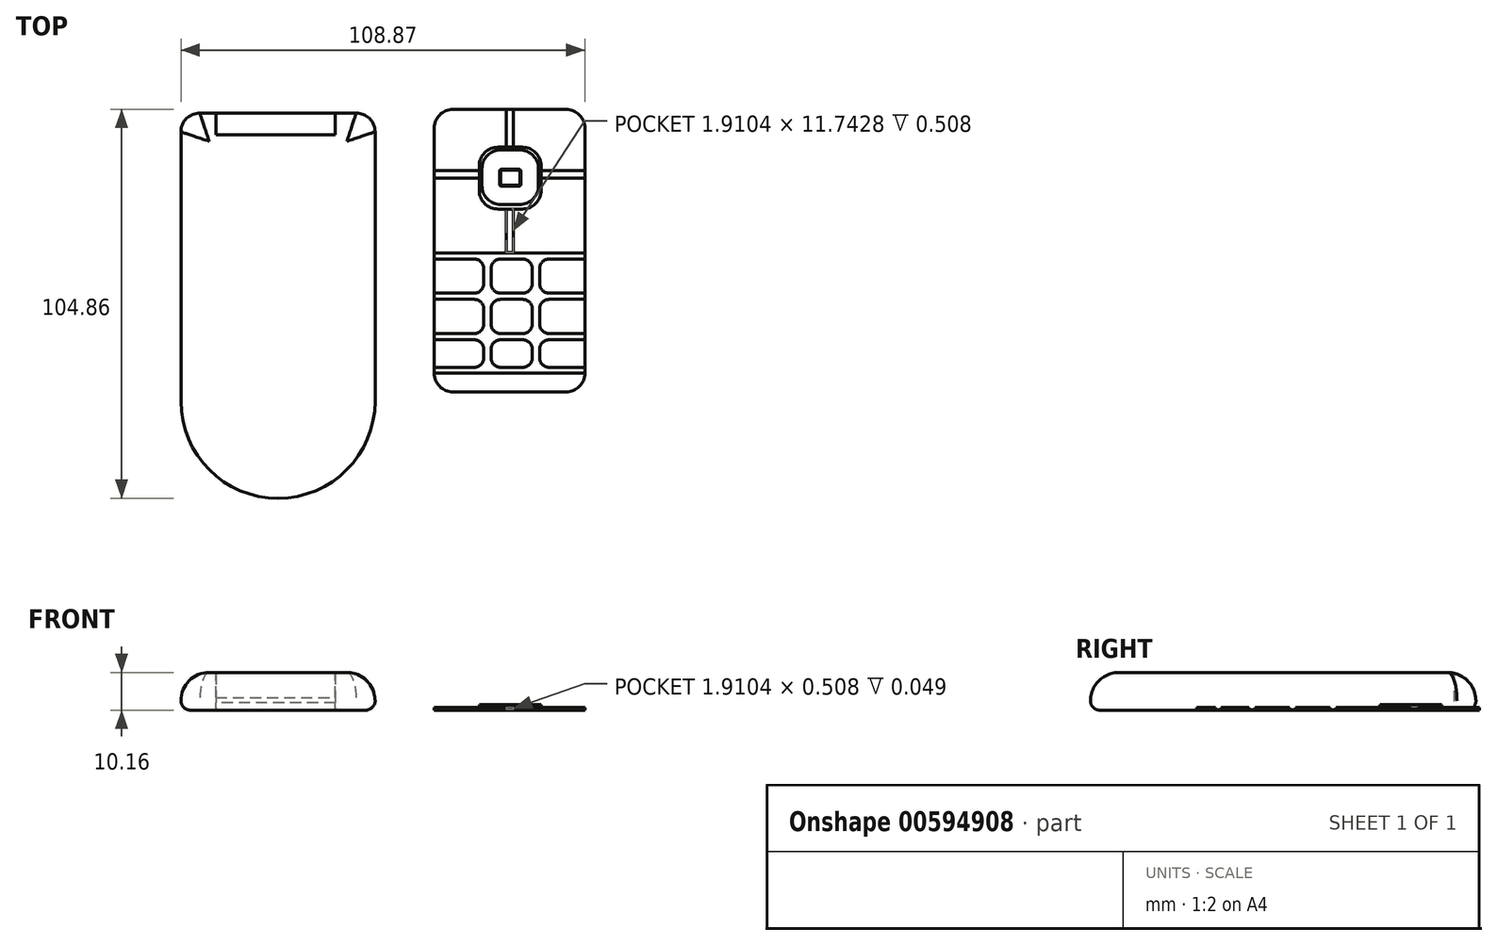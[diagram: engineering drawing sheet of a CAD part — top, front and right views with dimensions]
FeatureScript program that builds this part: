
annotation { "Feature Type Name" : "Feature", "Feature Type Description" : "" }
export const myFeature = defineFeature(function(context is Context, id is Id, definition is map)
    precondition{}
    {
        {
            var Q0;
            Q0=qCreatedBy(makeId("Top.planeOp"),FACE);
            var sketch = newSketch(context, id + "F0", { "sketchPlane" : qUnion([Q0])});
            skLineSegment(sketch, "E0.bottom", {"start": v(-38.75, 53.9) * mm, "end": v(13.57, 53.9) * mm});
            skLineSegment(sketch, "E0.top", {"start": v(-38.75, -49.98) * mm, "end": v(13.57, -49.98) * mm});
            skLineSegment(sketch, "E0.left", {"start": v(-38.75, 53.9) * mm, "end": v(-38.75, -49.98) * mm});
            skLineSegment(sketch, "E0.right", {"start": v(13.57, 53.9) * mm, "end": v(13.57, -49.98) * mm});
            skSolve(sketch);
        }
        {
            var Q0;
            Q0=makeQuery(id+"F0.imprint","IMPRINT",FACE,{"disambiguationData":[TD([[makeQuery(id+"F0.imprint","IMPRINT",EDGE,{"derivedFrom":sQuery(id+"F0.wireOp",EDGE,"E0.bottom")}),-1.0]])]});
            extrude(context, id + "F1", {"entities" : qUnion([Q0]), "depth" : 10.16 * mm, "offsetDistance" : 25.4 * mm});
        }
        {
            var Q0;
            Q0=makeQuery(id+"F1.opExtrude","SWEPT_EDGE",EDGE,{"disambiguationData":[OSD([sQuery(id+"F0.wireOp",EDGE,"E0.top"),sQuery(id+"F0.wireOp",EDGE,"E0.left")])]});
            var Q1;
            Q1=makeQuery(id+"F1.opExtrude","SWEPT_EDGE",EDGE,{"disambiguationData":[OSD([sQuery(id+"F0.wireOp",EDGE,"E0.top"),sQuery(id+"F0.wireOp",EDGE,"E0.right")])]});
            fillet(context, id + "F2", {"entities" : qUnion([Q0, Q1]), "radius" : 26.16 * mm, "tangentPropagation" : true, "allowEdgeOverflow" : false});
        }
        {
            var Q0;
            Q0=makeQuery(id+"F1.opExtrude","SWEPT_EDGE",EDGE,{"disambiguationData":[OSD([sQuery(id+"F0.wireOp",EDGE,"E0.bottom"),sQuery(id+"F0.wireOp",EDGE,"E0.left")])]});
            var Q1;
            Q1=makeQuery(id+"F1.opExtrude","SWEPT_EDGE",EDGE,{"disambiguationData":[OSD([sQuery(id+"F0.wireOp",EDGE,"E0.bottom"),sQuery(id+"F0.wireOp",EDGE,"E0.right")])]});
            fillet(context, id + "F3", {"entities" : qUnion([Q0, Q1]), "radius" : 5.08 * mm, "tangentPropagation" : true, "allowEdgeOverflow" : false});
        }
        {
            var Q0;
            Q0=makeQuery(id+"F1.opExtrude","CAP_EDGE",EDGE,{"disambiguationData":[OSD([sQuery(id+"F0.wireOp",EDGE,"E0.right")])],"isStart":false});
            fillet(context, id + "F4", {"entities" : qUnion([Q0]), "radius" : 7.62 * mm, "tangentPropagation" : true, "allowEdgeOverflow" : false});
        }
        {
            var Q0;
            Q0=makeQuery(id+"F1.opExtrude","CAP_EDGE",EDGE,{"disambiguationData":[OSD([sQuery(id+"F0.wireOp",EDGE,"E0.right")])],"isStart":true});
            fillet(context, id + "F5", {"entities" : qUnion([Q0]), "radius" : 2.54 * mm, "tangentPropagation" : true, "allowEdgeOverflow" : false});
        }
        {
            var Q0;
            Q0=qCreatedBy(makeId("Top.planeOp"),FACE);
            var sketch = newSketch(context, id + "F6", { "sketchPlane" : qUnion([Q0])});
            skLineSegment(sketch, "E1.bottom", {"start": v(29.48, -21.32) * mm, "end": v(70.12, -21.32) * mm});
            skLineSegment(sketch, "E1.top", {"start": v(29.48, 54.88) * mm, "end": v(70.12, 54.88) * mm});
            skLineSegment(sketch, "E1.left", {"start": v(29.48, -21.32) * mm, "end": v(29.48, 54.88) * mm});
            skLineSegment(sketch, "E1.right", {"start": v(70.12, -21.32) * mm, "end": v(70.12, 54.88) * mm});
            skSolve(sketch);
        }
        {
            var Q0;
            Q0=makeQuery(id+"F6.imprint","IMPRINT",FACE,{"disambiguationData":[TD([[makeQuery(id+"F6.imprint","IMPRINT",EDGE,{"derivedFrom":sQuery(id+"F6.wireOp",EDGE,"E1.bottom")}),1.0]])]});
            extrude(context, id + "F7", {"entities" : qUnion([Q0]), "depth" : 0.76 * mm, "offsetDistance" : 25.4 * mm});
        }
        {
            var Q0;
            Q0=makeQuery(id+"F7.opExtrude","SWEPT_EDGE",EDGE,{"disambiguationData":[OSD([sQuery(id+"F6.wireOp",EDGE,"E1.top"),sQuery(id+"F6.wireOp",EDGE,"E1.left")])]});
            var Q1;
            Q1=makeQuery(id+"F7.opExtrude","SWEPT_EDGE",EDGE,{"disambiguationData":[OSD([sQuery(id+"F6.wireOp",EDGE,"E1.top"),sQuery(id+"F6.wireOp",EDGE,"E1.right")])]});
            var Q2;
            Q2=makeQuery(id+"F7.opExtrude","SWEPT_EDGE",EDGE,{"disambiguationData":[OSD([sQuery(id+"F6.wireOp",EDGE,"E1.bottom"),sQuery(id+"F6.wireOp",EDGE,"E1.left")])]});
            var Q3;
            Q3=makeQuery(id+"F7.opExtrude","SWEPT_EDGE",EDGE,{"disambiguationData":[OSD([sQuery(id+"F6.wireOp",EDGE,"E1.bottom"),sQuery(id+"F6.wireOp",EDGE,"E1.right")])]});
            fillet(context, id + "F8", {"entities" : qUnion([Q0, Q1, Q2, Q3]), "radius" : 5.08 * mm, "tangentPropagation" : true, "allowEdgeOverflow" : false});
        }
        {
            var Q0;
            Q0=makeQuery(id+"F7.opExtrude","CAP_FACE",FACE,{"disambiguationData":[OSD([sQuery(id+"F6.wireOp",EDGE,"E1.bottom"),sQuery(id+"F6.wireOp",EDGE,"E1.top"),sQuery(id+"F6.wireOp",EDGE,"E1.left"),sQuery(id+"F6.wireOp",EDGE,"E1.right")])],"isStart":false});
            var sketch = newSketch(context, id + "F9", { "sketchPlane" : qUnion([Q0])});
            skLineSegment(sketch, "E2", {"start": v(29.48, 16.2) * mm, "end": v(70.12, 16.2) * mm});
            skLineSegment(sketch, "E3", {"start": v(29.48, 5.31) * mm, "end": v(70.12, 5.31) * mm});
            skLineSegment(sketch, "E4", {"start": v(29.48, -5.57) * mm, "end": v(70.12, -5.57) * mm});
            skLineSegment(sketch, "E5", {"start": v(29.48, -16.24) * mm, "end": v(70.12, -16.24) * mm});
            skLineSegment(sketch, "E6", {"start": v(29.48, 14.53) * mm, "end": v(70.12, 14.53) * mm});
            skLineSegment(sketch, "E7", {"start": v(29.48, 3.64) * mm, "end": v(70.12, 3.64) * mm});
            skLineSegment(sketch, "E8", {"start": v(29.48, -7.24) * mm, "end": v(70.12, -7.24) * mm});
            skLineSegment(sketch, "E9", {"start": v(29.48, 16.2) * mm, "end": v(29.48, 14.53) * mm});
            skLineSegment(sketch, "E10", {"start": v(29.48, 5.31) * mm, "end": v(29.48, 3.64) * mm});
            skLineSegment(sketch, "E11", {"start": v(29.48, -5.57) * mm, "end": v(29.48, -7.24) * mm});
            skLineSegment(sketch, "E12", {"start": v(70.12, -5.57) * mm, "end": v(70.12, -7.24) * mm});
            skLineSegment(sketch, "E13", {"start": v(70.12, 5.31) * mm, "end": v(70.12, 3.64) * mm});
            skLineSegment(sketch, "E14", {"start": v(70.12, 16.2) * mm, "end": v(70.12, 14.53) * mm});
            skLineSegment(sketch, "E15", {"start": v(42.84, 16.2) * mm, "end": v(42.84, -16.24) * mm});
            skLineSegment(sketch, "E16", {"start": v(42.84, -16.24) * mm, "end": v(44.85, -16.24) * mm});
            skLineSegment(sketch, "E17", {"start": v(44.85, -16.24) * mm, "end": v(44.85, 16.2) * mm});
            skLineSegment(sketch, "E18", {"start": v(44.85, 16.2) * mm, "end": v(55.9, 16.2) * mm});
            skLineSegment(sketch, "E19", {"start": v(55.9, 16.2) * mm, "end": v(55.9, -16.24) * mm});
            skLineSegment(sketch, "E20", {"start": v(55.9, -16.24) * mm, "end": v(57.92, -16.24) * mm});
            skLineSegment(sketch, "E21", {"start": v(57.92, -16.24) * mm, "end": v(57.92, 16.2) * mm});
            skLineSegment(sketch, "E22", {"start": v(55.9, 16.2) * mm, "end": v(57.92, 16.2) * mm});
            skLineSegment(sketch, "E23", {"start": v(44.85, 16.2) * mm, "end": v(42.84, 16.2) * mm});
            skLineSegment(sketch, "E24", {"start": v(55.9, -16.24) * mm, "end": v(55.9, -19.8) * mm});
            skLineSegment(sketch, "E25", {"start": v(55.9, -19.8) * mm, "end": v(57.92, -16.24) * mm});
            skLineSegment(sketch, "E26", {"start": v(42.84, -16.24) * mm, "end": v(42.84, -19.8) * mm});
            skLineSegment(sketch, "E27", {"start": v(42.84, -19.8) * mm, "end": v(44.85, -16.24) * mm});
            skLineSegment(sketch, "E28", {"start": v(29.48, -14.7) * mm, "end": v(70.12, -14.7) * mm});
            skLineSegment(sketch, "E29", {"start": v(29.48, -14.7) * mm, "end": v(29.48, -16.24) * mm});
            skLineSegment(sketch, "E30", {"start": v(70.12, -14.7) * mm, "end": v(70.12, -16.24) * mm});
            skSolve(sketch);
        }
        {
            var Q0;
            {var subQ0=sQuery(id+"F9.wireOp",EDGE,"E9");Q0=makeQuery(id+"F9.imprint","IMPRINT",FACE,{"disambiguationData":[TD([[makeQuery(id+"F9.imprint","IMPRINT",EDGE,{"derivedFrom":subQ0}),-1.0]])]});}
            var Q1;
            {var subQ0=sQuery(id+"F9.wireOp",EDGE,"E17");var subQ1=sQuery(id+"F9.wireOp",EDGE,"E2");var subQ2=makeQuery(id+"F9.imprint","INTERSECT",VERTEX,{"derivedFrom":[subQ1,subQ0]});Q1=makeQuery(id+"F9.imprint","IMPRINT",FACE,{"disambiguationData":[TD([[makeQuery(id+"F9.imprint","IMPRINT",EDGE,{"disambiguationData":[TD([[subQ2,-1.0]])],"derivedFrom":subQ1}),-1.0]])]});}
            var Q2;
            {var subQ0=sQuery(id+"F9.wireOp",EDGE,"E14");Q2=makeQuery(id+"F9.imprint","IMPRINT",FACE,{"disambiguationData":[TD([[makeQuery(id+"F9.imprint","IMPRINT",EDGE,{"derivedFrom":subQ0}),1.0]])]});}
            var Q3;
            {var subQ0=sQuery(id+"F9.wireOp",EDGE,"E13");Q3=makeQuery(id+"F9.imprint","IMPRINT",FACE,{"disambiguationData":[TD([[makeQuery(id+"F9.imprint","IMPRINT",EDGE,{"derivedFrom":subQ0}),1.0]])]});}
            var Q4;
            {var subQ0=sQuery(id+"F9.wireOp",EDGE,"E17");var subQ1=sQuery(id+"F9.wireOp",EDGE,"E3");var subQ2=makeQuery(id+"F9.imprint","INTERSECT",VERTEX,{"derivedFrom":[subQ1,subQ0]});Q4=makeQuery(id+"F9.imprint","IMPRINT",FACE,{"disambiguationData":[TD([[makeQuery(id+"F9.imprint","IMPRINT",EDGE,{"disambiguationData":[TD([[subQ2,-1.0]])],"derivedFrom":subQ1}),-1.0]])]});}
            var Q5;
            {var subQ0=sQuery(id+"F9.wireOp",EDGE,"E10");Q5=makeQuery(id+"F9.imprint","IMPRINT",FACE,{"disambiguationData":[TD([[makeQuery(id+"F9.imprint","IMPRINT",EDGE,{"derivedFrom":subQ0}),-1.0]])]});}
            var Q6;
            {var subQ0=sQuery(id+"F9.wireOp",EDGE,"E11");Q6=makeQuery(id+"F9.imprint","IMPRINT",FACE,{"disambiguationData":[TD([[makeQuery(id+"F9.imprint","IMPRINT",EDGE,{"derivedFrom":subQ0}),-1.0]])]});}
            var Q7;
            {var subQ0=sQuery(id+"F9.wireOp",EDGE,"E17");var subQ1=sQuery(id+"F9.wireOp",EDGE,"E4");var subQ2=makeQuery(id+"F9.imprint","INTERSECT",VERTEX,{"derivedFrom":[subQ1,subQ0]});Q7=makeQuery(id+"F9.imprint","IMPRINT",FACE,{"disambiguationData":[TD([[makeQuery(id+"F9.imprint","IMPRINT",EDGE,{"disambiguationData":[TD([[subQ2,-1.0]])],"derivedFrom":subQ1}),-1.0]])]});}
            var Q8;
            {var subQ3=sQuery(id+"F9.wireOp",EDGE,"E12");Q8=makeQuery(id+"F9.imprint","IMPRINT",FACE,{"disambiguationData":[TD([[makeQuery(id+"F9.imprint","IMPRINT",EDGE,{"derivedFrom":subQ3}),1.0]])]});}
            var Q9;
            {var subQ0=sQuery(id+"F9.wireOp",EDGE,"E21");var subQ1=sQuery(id+"F9.wireOp",EDGE,"E4");var subQ2=makeQuery(id+"F9.imprint","INTERSECT",VERTEX,{"derivedFrom":[subQ1,subQ0]});Q9=makeQuery(id+"F9.imprint","IMPRINT",FACE,{"disambiguationData":[TD([[makeQuery(id+"F9.imprint","IMPRINT",EDGE,{"disambiguationData":[TD([[subQ2,1.0]])],"derivedFrom":subQ1}),1.0]])]});}
            var Q10;
            {var subQ0=sQuery(id+"F9.wireOp",EDGE,"E21");var subQ1=sQuery(id+"F9.wireOp",EDGE,"E4");var subQ2=makeQuery(id+"F9.imprint","INTERSECT",VERTEX,{"derivedFrom":[subQ1,subQ0]});Q10=makeQuery(id+"F9.imprint","IMPRINT",FACE,{"disambiguationData":[TD([[makeQuery(id+"F9.imprint","IMPRINT",EDGE,{"disambiguationData":[TD([[subQ2,1.0]])],"derivedFrom":subQ1}),-1.0]])]});}
            var Q11;
            {var subQ5=sQuery(id+"F9.wireOp",EDGE,"E20");Q11=makeQuery(id+"F9.imprint","IMPRINT",FACE,{"disambiguationData":[TD([[makeQuery(id+"F9.imprint","IMPRINT",EDGE,{"derivedFrom":subQ5}),1.0]])]});}
            var Q12;
            {var subQ0=sQuery(id+"F9.wireOp",EDGE,"E21");var subQ1=sQuery(id+"F9.wireOp",EDGE,"E3");var subQ2=makeQuery(id+"F9.imprint","INTERSECT",VERTEX,{"derivedFrom":[subQ1,subQ0]});Q12=makeQuery(id+"F9.imprint","IMPRINT",FACE,{"disambiguationData":[TD([[makeQuery(id+"F9.imprint","IMPRINT",EDGE,{"disambiguationData":[TD([[subQ2,1.0]])],"derivedFrom":subQ1}),-1.0]])]});}
            var Q13;
            {var subQ0=sQuery(id+"F9.wireOp",EDGE,"E21");var subQ1=sQuery(id+"F9.wireOp",EDGE,"E3");var subQ2=makeQuery(id+"F9.imprint","INTERSECT",VERTEX,{"derivedFrom":[subQ1,subQ0]});Q13=makeQuery(id+"F9.imprint","IMPRINT",FACE,{"disambiguationData":[TD([[makeQuery(id+"F9.imprint","IMPRINT",EDGE,{"disambiguationData":[TD([[subQ2,1.0]])],"derivedFrom":subQ1}),1.0]])]});}
            var Q14;
            {var subQ0=sQuery(id+"F9.wireOp",EDGE,"E21");var subQ1=sQuery(id+"F9.wireOp",EDGE,"E2");var subQ2=makeQuery(id+"F9.imprint","INTERSECT",VERTEX,{"derivedFrom":[subQ1,subQ0]});Q14=makeQuery(id+"F9.imprint","IMPRINT",FACE,{"disambiguationData":[TD([[makeQuery(id+"F9.imprint","IMPRINT",EDGE,{"disambiguationData":[TD([[subQ2,1.0]])],"derivedFrom":subQ1}),-1.0]])]});}
            var Q15;
            {var subQ0=sQuery(id+"F9.wireOp",EDGE,"E17");var subQ1=sQuery(id+"F9.wireOp",EDGE,"E2");var subQ2=makeQuery(id+"F9.imprint","INTERSECT",VERTEX,{"derivedFrom":[subQ1,subQ0]});Q15=makeQuery(id+"F9.imprint","IMPRINT",FACE,{"disambiguationData":[TD([[makeQuery(id+"F9.imprint","IMPRINT",EDGE,{"disambiguationData":[TD([[subQ2,1.0]])],"derivedFrom":subQ1}),-1.0]])]});}
            var Q16;
            {var subQ0=sQuery(id+"F9.wireOp",EDGE,"E17");var subQ1=sQuery(id+"F9.wireOp",EDGE,"E3");var subQ2=makeQuery(id+"F9.imprint","INTERSECT",VERTEX,{"derivedFrom":[subQ1,subQ0]});Q16=makeQuery(id+"F9.imprint","IMPRINT",FACE,{"disambiguationData":[TD([[makeQuery(id+"F9.imprint","IMPRINT",EDGE,{"disambiguationData":[TD([[subQ2,1.0]])],"derivedFrom":subQ1}),1.0]])]});}
            var Q17;
            {var subQ0=sQuery(id+"F9.wireOp",EDGE,"E17");var subQ1=sQuery(id+"F9.wireOp",EDGE,"E3");var subQ2=makeQuery(id+"F9.imprint","INTERSECT",VERTEX,{"derivedFrom":[subQ1,subQ0]});Q17=makeQuery(id+"F9.imprint","IMPRINT",FACE,{"disambiguationData":[TD([[makeQuery(id+"F9.imprint","IMPRINT",EDGE,{"disambiguationData":[TD([[subQ2,1.0]])],"derivedFrom":subQ1}),-1.0]])]});}
            var Q18;
            {var subQ0=sQuery(id+"F9.wireOp",EDGE,"E15");var subQ1=sQuery(id+"F9.wireOp",EDGE,"E4");var subQ2=makeQuery(id+"F9.imprint","INTERSECT",VERTEX,{"derivedFrom":[subQ1,subQ0]});Q18=makeQuery(id+"F9.imprint","IMPRINT",FACE,{"disambiguationData":[TD([[makeQuery(id+"F9.imprint","IMPRINT",EDGE,{"disambiguationData":[TD([[subQ2,-1.0]])],"derivedFrom":subQ1}),1.0]])]});}
            var Q19;
            {var subQ0=sQuery(id+"F9.wireOp",EDGE,"E15");var subQ1=sQuery(id+"F9.wireOp",EDGE,"E4");var subQ2=makeQuery(id+"F9.imprint","INTERSECT",VERTEX,{"derivedFrom":[subQ1,subQ0]});Q19=makeQuery(id+"F9.imprint","IMPRINT",FACE,{"disambiguationData":[TD([[makeQuery(id+"F9.imprint","IMPRINT",EDGE,{"disambiguationData":[TD([[subQ2,-1.0]])],"derivedFrom":subQ1}),-1.0]])]});}
            var Q20;
            {var subQ5=sQuery(id+"F9.wireOp",EDGE,"E16");Q20=makeQuery(id+"F9.imprint","IMPRINT",FACE,{"disambiguationData":[TD([[makeQuery(id+"F9.imprint","IMPRINT",EDGE,{"derivedFrom":subQ5}),1.0]])]});}
            var Q21;
            {var subQ0=sQuery(id+"F9.wireOp",EDGE,"E29");Q21=makeQuery(id+"F9.imprint","IMPRINT",FACE,{"disambiguationData":[TD([[makeQuery(id+"F9.imprint","IMPRINT",EDGE,{"derivedFrom":subQ0}),-1.0]])]});}
            var Q22;
            {var subQ0=sQuery(id+"F9.wireOp",EDGE,"E17");var subQ1=sQuery(id+"F9.wireOp",EDGE,"E8");var subQ2=makeQuery(id+"F9.imprint","INTERSECT",VERTEX,{"derivedFrom":[subQ1,subQ0]});Q22=makeQuery(id+"F9.imprint","IMPRINT",FACE,{"disambiguationData":[TD([[makeQuery(id+"F9.imprint","IMPRINT",EDGE,{"disambiguationData":[TD([[subQ2,1.0]])],"derivedFrom":subQ1}),-1.0]])]});}
            var Q23;
            {var subQ0=sQuery(id+"F9.wireOp",EDGE,"E17");var subQ5=sQuery(id+"F9.wireOp",EDGE,"E28");var subQ6=makeQuery(id+"F9.imprint","INTERSECT",VERTEX,{"derivedFrom":[subQ0,subQ5]});Q23=makeQuery(id+"F9.imprint","IMPRINT",FACE,{"disambiguationData":[TD([[makeQuery(id+"F9.imprint","IMPRINT",EDGE,{"disambiguationData":[TD([[subQ6,1.0]])],"derivedFrom":subQ5}),-1.0]])]});}
            var Q24;
            {var subQ0=sQuery(id+"F9.wireOp",EDGE,"E17");var subQ5=sQuery(id+"F9.wireOp",EDGE,"E28");var subQ6=makeQuery(id+"F9.imprint","INTERSECT",VERTEX,{"derivedFrom":[subQ0,subQ5]});Q24=makeQuery(id+"F9.imprint","IMPRINT",FACE,{"disambiguationData":[TD([[makeQuery(id+"F9.imprint","IMPRINT",EDGE,{"disambiguationData":[TD([[subQ6,-1.0]])],"derivedFrom":subQ5}),-1.0]])]});}
            var Q25;
            {var subQ3=sQuery(id+"F9.wireOp",EDGE,"E21");var subQ5=sQuery(id+"F9.wireOp",EDGE,"E28");var subQ6=makeQuery(id+"F9.imprint","INTERSECT",VERTEX,{"derivedFrom":[subQ3,subQ5]});Q25=makeQuery(id+"F9.imprint","IMPRINT",FACE,{"disambiguationData":[TD([[makeQuery(id+"F9.imprint","IMPRINT",EDGE,{"disambiguationData":[TD([[subQ6,1.0]])],"derivedFrom":subQ5}),-1.0]])]});}
            var Q26;
            {var subQ0=sQuery(id+"F9.wireOp",EDGE,"E21");var subQ1=sQuery(id+"F9.wireOp",EDGE,"E8");var subQ2=makeQuery(id+"F9.imprint","INTERSECT",VERTEX,{"derivedFrom":[subQ1,subQ0]});Q26=makeQuery(id+"F9.imprint","IMPRINT",FACE,{"disambiguationData":[TD([[makeQuery(id+"F9.imprint","IMPRINT",EDGE,{"disambiguationData":[TD([[subQ2,1.0]])],"derivedFrom":subQ1}),-1.0]])]});}
            var Q27;
            {var subQ0=sQuery(id+"F9.wireOp",EDGE,"E30");Q27=makeQuery(id+"F9.imprint","IMPRINT",FACE,{"disambiguationData":[TD([[makeQuery(id+"F9.imprint","IMPRINT",EDGE,{"derivedFrom":subQ0}),1.0]])]});}
            extrude(context, id + "F10", {"entities" : qUnion([Q0, Q1, Q2, Q3, Q4, Q5, Q6, Q7, Q8, Q9, Q10, Q11, Q12, Q13, Q14, Q15, Q16, Q17, Q18, Q19, Q20, Q21, Q22, Q23, Q24, Q25, Q26, Q27]), "operationType" : NewBodyOperationType.REMOVE, "oppositeDirection" : true, "depth" : 0.6 * mm, "offsetDistance" : 25.4 * mm});
        }
        {
            var Q0;
            Q0=makeQuery(id+"F10.boolean.opBoolean","COPY",EDGE,{"derivedFrom":makeQuery(id+"F10.opExtrude","SWEPT_EDGE",EDGE,{"disambiguationData":[OSD([sQuery(id+"F6.wireOp",EDGE,"E1.right"),sQuery(id+"F9.wireOp",EDGE,"E28"),sQuery(id+"F9.wireOp",EDGE,"E30")])]})});
            var Q1;
            Q1=makeQuery(id+"F10.boolean.opBoolean","COPY",EDGE,{"derivedFrom":makeQuery(id+"F10.opExtrude","SWEPT_EDGE",EDGE,{"disambiguationData":[OSD([sQuery(id+"F6.wireOp",EDGE,"E1.right"),sQuery(id+"F9.wireOp",EDGE,"E4"),sQuery(id+"F9.wireOp",EDGE,"E12")])]})});
            var Q2;
            Q2=makeQuery(id+"F10.boolean.opBoolean","COPY",EDGE,{"derivedFrom":makeQuery(id+"F10.opExtrude","SWEPT_EDGE",EDGE,{"disambiguationData":[OSD([sQuery(id+"F9.wireOp",EDGE,"E19"),sQuery(id+"F9.wireOp",EDGE,"E28")])]})});
            var Q3;
            Q3=makeQuery(id+"F10.boolean.opBoolean","COPY",EDGE,{"derivedFrom":makeQuery(id+"F10.opExtrude","SWEPT_EDGE",EDGE,{"disambiguationData":[OSD([sQuery(id+"F9.wireOp",EDGE,"E4"),sQuery(id+"F9.wireOp",EDGE,"E19")])]})});
            var Q4;
            Q4=makeQuery(id+"F10.boolean.opBoolean","COPY",EDGE,{"derivedFrom":makeQuery(id+"F10.opExtrude","SWEPT_EDGE",EDGE,{"disambiguationData":[OSD([sQuery(id+"F9.wireOp",EDGE,"E7"),sQuery(id+"F9.wireOp",EDGE,"E19")])]})});
            var Q5;
            Q5=makeQuery(id+"F10.boolean.opBoolean","COPY",EDGE,{"derivedFrom":makeQuery(id+"F10.opExtrude","SWEPT_EDGE",EDGE,{"disambiguationData":[OSD([sQuery(id+"F9.wireOp",EDGE,"E3"),sQuery(id+"F9.wireOp",EDGE,"E19")])]})});
            var Q6;
            Q6=makeQuery(id+"F10.boolean.opBoolean","COPY",EDGE,{"derivedFrom":makeQuery(id+"F10.opExtrude","SWEPT_EDGE",EDGE,{"disambiguationData":[OSD([sQuery(id+"F9.wireOp",EDGE,"E6"),sQuery(id+"F9.wireOp",EDGE,"E19")])]})});
            var Q7;
            Q7=makeQuery(id+"F10.boolean.opBoolean","COPY",EDGE,{"derivedFrom":makeQuery(id+"F10.opExtrude","SWEPT_EDGE",EDGE,{"disambiguationData":[OSD([sQuery(id+"F9.wireOp",EDGE,"E15"),sQuery(id+"F9.wireOp",EDGE,"E28")])]})});
            var Q8;
            Q8=makeQuery(id+"F10.boolean.opBoolean","COPY",EDGE,{"derivedFrom":makeQuery(id+"F10.opExtrude","SWEPT_EDGE",EDGE,{"disambiguationData":[OSD([sQuery(id+"F9.wireOp",EDGE,"E4"),sQuery(id+"F9.wireOp",EDGE,"E15")])]})});
            var Q9;
            Q9=makeQuery(id+"F10.boolean.opBoolean","COPY",EDGE,{"derivedFrom":makeQuery(id+"F10.opExtrude","SWEPT_EDGE",EDGE,{"disambiguationData":[OSD([sQuery(id+"F9.wireOp",EDGE,"E7"),sQuery(id+"F9.wireOp",EDGE,"E15")])]})});
            var Q10;
            Q10=makeQuery(id+"F10.boolean.opBoolean","COPY",EDGE,{"derivedFrom":makeQuery(id+"F10.opExtrude","SWEPT_EDGE",EDGE,{"disambiguationData":[OSD([sQuery(id+"F9.wireOp",EDGE,"E3"),sQuery(id+"F9.wireOp",EDGE,"E15")])]})});
            var Q11;
            Q11=makeQuery(id+"F10.boolean.opBoolean","COPY",EDGE,{"derivedFrom":makeQuery(id+"F10.opExtrude","SWEPT_EDGE",EDGE,{"disambiguationData":[OSD([sQuery(id+"F9.wireOp",EDGE,"E3"),sQuery(id+"F9.wireOp",EDGE,"E17")])]})});
            var Q12;
            Q12=makeQuery(id+"F10.boolean.opBoolean","COPY",EDGE,{"derivedFrom":makeQuery(id+"F10.opExtrude","SWEPT_EDGE",EDGE,{"disambiguationData":[OSD([sQuery(id+"F9.wireOp",EDGE,"E4"),sQuery(id+"F9.wireOp",EDGE,"E17")])]})});
            var Q13;
            Q13=makeQuery(id+"F10.boolean.opBoolean","COPY",EDGE,{"derivedFrom":makeQuery(id+"F10.opExtrude","SWEPT_EDGE",EDGE,{"disambiguationData":[OSD([sQuery(id+"F9.wireOp",EDGE,"E17"),sQuery(id+"F9.wireOp",EDGE,"E28")])]})});
            var Q14;
            Q14=makeQuery(id+"F10.boolean.opBoolean","COPY",EDGE,{"derivedFrom":makeQuery(id+"F10.opExtrude","SWEPT_EDGE",EDGE,{"disambiguationData":[OSD([sQuery(id+"F6.wireOp",EDGE,"E1.left"),sQuery(id+"F9.wireOp",EDGE,"E28"),sQuery(id+"F9.wireOp",EDGE,"E29")])]})});
            var Q15;
            Q15=makeQuery(id+"F10.boolean.opBoolean","COPY",EDGE,{"derivedFrom":makeQuery(id+"F10.opExtrude","SWEPT_EDGE",EDGE,{"disambiguationData":[OSD([sQuery(id+"F9.wireOp",EDGE,"E21"),sQuery(id+"F9.wireOp",EDGE,"E28")])]})});
            var Q16;
            Q16=makeQuery(id+"F10.boolean.opBoolean","COPY",EDGE,{"derivedFrom":makeQuery(id+"F10.opExtrude","SWEPT_EDGE",EDGE,{"disambiguationData":[OSD([sQuery(id+"F9.wireOp",EDGE,"E4"),sQuery(id+"F9.wireOp",EDGE,"E21")])]})});
            var Q17;
            Q17=makeQuery(id+"F10.boolean.opBoolean","COPY",EDGE,{"derivedFrom":makeQuery(id+"F10.opExtrude","SWEPT_EDGE",EDGE,{"disambiguationData":[OSD([sQuery(id+"F9.wireOp",EDGE,"E3"),sQuery(id+"F9.wireOp",EDGE,"E21")])]})});
            var Q18;
            Q18=makeQuery(id+"F10.boolean.opBoolean","COPY",EDGE,{"derivedFrom":makeQuery(id+"F10.opExtrude","SWEPT_EDGE",EDGE,{"disambiguationData":[OSD([sQuery(id+"F9.wireOp",EDGE,"E8"),sQuery(id+"F9.wireOp",EDGE,"E17")])]})});
            var Q19;
            Q19=makeQuery(id+"F10.boolean.opBoolean","COPY",EDGE,{"derivedFrom":makeQuery(id+"F10.opExtrude","SWEPT_EDGE",EDGE,{"disambiguationData":[OSD([sQuery(id+"F9.wireOp",EDGE,"E7"),sQuery(id+"F9.wireOp",EDGE,"E17")])]})});
            var Q20;
            Q20=makeQuery(id+"F10.boolean.opBoolean","COPY",EDGE,{"derivedFrom":makeQuery(id+"F10.opExtrude","SWEPT_EDGE",EDGE,{"disambiguationData":[OSD([sQuery(id+"F9.wireOp",EDGE,"E6"),sQuery(id+"F9.wireOp",EDGE,"E17")])]})});
            var Q21;
            Q21=makeQuery(id+"F10.boolean.opBoolean","COPY",EDGE,{"derivedFrom":makeQuery(id+"F10.opExtrude","SWEPT_EDGE",EDGE,{"disambiguationData":[OSD([sQuery(id+"F9.wireOp",EDGE,"E6"),sQuery(id+"F9.wireOp",EDGE,"E21")])]})});
            var Q22;
            Q22=makeQuery(id+"F10.boolean.opBoolean","COPY",EDGE,{"derivedFrom":makeQuery(id+"F10.opExtrude","SWEPT_EDGE",EDGE,{"disambiguationData":[OSD([sQuery(id+"F9.wireOp",EDGE,"E8"),sQuery(id+"F9.wireOp",EDGE,"E19")])]})});
            var Q23;
            Q23=makeQuery(id+"F10.boolean.opBoolean","COPY",EDGE,{"derivedFrom":makeQuery(id+"F10.opExtrude","SWEPT_EDGE",EDGE,{"disambiguationData":[OSD([sQuery(id+"F9.wireOp",EDGE,"E8"),sQuery(id+"F9.wireOp",EDGE,"E21")])]})});
            var Q24;
            Q24=makeQuery(id+"F10.boolean.opBoolean","COPY",EDGE,{"derivedFrom":makeQuery(id+"F10.opExtrude","SWEPT_EDGE",EDGE,{"disambiguationData":[OSD([sQuery(id+"F9.wireOp",EDGE,"E7"),sQuery(id+"F9.wireOp",EDGE,"E21")])]})});
            var Q25;
            Q25=makeQuery(id+"F10.boolean.opBoolean","COPY",EDGE,{"derivedFrom":makeQuery(id+"F10.opExtrude","SWEPT_EDGE",EDGE,{"disambiguationData":[OSD([sQuery(id+"F9.wireOp",EDGE,"E6"),sQuery(id+"F9.wireOp",EDGE,"E15")])]})});
            var Q26;
            Q26=makeQuery(id+"F10.boolean.opBoolean","COPY",EDGE,{"derivedFrom":makeQuery(id+"F10.opExtrude","SWEPT_EDGE",EDGE,{"disambiguationData":[OSD([sQuery(id+"F6.wireOp",EDGE,"E1.left"),sQuery(id+"F9.wireOp",EDGE,"E6"),sQuery(id+"F9.wireOp",EDGE,"E9")])]})});
            var Q27;
            Q27=makeQuery(id+"F10.boolean.opBoolean","COPY",EDGE,{"derivedFrom":makeQuery(id+"F10.opExtrude","SWEPT_EDGE",EDGE,{"disambiguationData":[OSD([sQuery(id+"F6.wireOp",EDGE,"E1.left"),sQuery(id+"F9.wireOp",EDGE,"E3"),sQuery(id+"F9.wireOp",EDGE,"E10")])]})});
            var Q28;
            Q28=makeQuery(id+"F10.boolean.opBoolean","COPY",EDGE,{"derivedFrom":makeQuery(id+"F10.opExtrude","SWEPT_EDGE",EDGE,{"disambiguationData":[OSD([sQuery(id+"F6.wireOp",EDGE,"E1.left"),sQuery(id+"F9.wireOp",EDGE,"E7"),sQuery(id+"F9.wireOp",EDGE,"E10")])]})});
            var Q29;
            Q29=makeQuery(id+"F10.boolean.opBoolean","COPY",EDGE,{"derivedFrom":makeQuery(id+"F10.opExtrude","SWEPT_EDGE",EDGE,{"disambiguationData":[OSD([sQuery(id+"F6.wireOp",EDGE,"E1.left"),sQuery(id+"F9.wireOp",EDGE,"E4"),sQuery(id+"F9.wireOp",EDGE,"E11")])]})});
            var Q30;
            Q30=makeQuery(id+"F10.boolean.opBoolean","COPY",EDGE,{"derivedFrom":makeQuery(id+"F10.opExtrude","SWEPT_EDGE",EDGE,{"disambiguationData":[OSD([sQuery(id+"F6.wireOp",EDGE,"E1.left"),sQuery(id+"F9.wireOp",EDGE,"E8"),sQuery(id+"F9.wireOp",EDGE,"E11")])]})});
            var Q31;
            Q31=makeQuery(id+"F10.boolean.opBoolean","COPY",EDGE,{"derivedFrom":makeQuery(id+"F10.opExtrude","SWEPT_EDGE",EDGE,{"disambiguationData":[OSD([sQuery(id+"F9.wireOp",EDGE,"E8"),sQuery(id+"F9.wireOp",EDGE,"E15")])]})});
            var Q32;
            Q32=makeQuery(id+"F10.boolean.opBoolean","COPY",EDGE,{"derivedFrom":makeQuery(id+"F10.opExtrude","SWEPT_EDGE",EDGE,{"disambiguationData":[OSD([sQuery(id+"F6.wireOp",EDGE,"E1.right"),sQuery(id+"F9.wireOp",EDGE,"E6"),sQuery(id+"F9.wireOp",EDGE,"E14")])]})});
            var Q33;
            Q33=makeQuery(id+"F10.boolean.opBoolean","COPY",EDGE,{"derivedFrom":makeQuery(id+"F10.opExtrude","SWEPT_EDGE",EDGE,{"disambiguationData":[OSD([sQuery(id+"F6.wireOp",EDGE,"E1.right"),sQuery(id+"F9.wireOp",EDGE,"E3"),sQuery(id+"F9.wireOp",EDGE,"E13")])]})});
            var Q34;
            Q34=makeQuery(id+"F10.boolean.opBoolean","COPY",EDGE,{"derivedFrom":makeQuery(id+"F10.opExtrude","SWEPT_EDGE",EDGE,{"disambiguationData":[OSD([sQuery(id+"F6.wireOp",EDGE,"E1.right"),sQuery(id+"F9.wireOp",EDGE,"E7"),sQuery(id+"F9.wireOp",EDGE,"E13")])]})});
            var Q35;
            Q35=makeQuery(id+"F10.boolean.opBoolean","COPY",EDGE,{"derivedFrom":makeQuery(id+"F10.opExtrude","SWEPT_EDGE",EDGE,{"disambiguationData":[OSD([sQuery(id+"F6.wireOp",EDGE,"E1.right"),sQuery(id+"F9.wireOp",EDGE,"E8"),sQuery(id+"F9.wireOp",EDGE,"E12")])]})});
            fillet(context, id + "F11", {"entities" : qUnion([Q0, Q1, Q2, Q3, Q4, Q5, Q6, Q7, Q8, Q9, Q10, Q11, Q12, Q13, Q14, Q15, Q16, Q17, Q18, Q19, Q20, Q21, Q22, Q23, Q24, Q25, Q26, Q27, Q28, Q29, Q30, Q31, Q32, Q33, Q34, Q35]), "radius" : 2.54 * mm, "tangentPropagation" : true, "allowEdgeOverflow" : false});
        }
        {
            var Q0;
            {var subQ0=sQuery(id+"F6.wireOp",EDGE,"E1.right");var subQ1=sQuery(id+"F6.wireOp",EDGE,"E1.left");var subQ2=sQuery(id+"F6.wireOp",EDGE,"E1.top");Q0=makeQuery(id+"F10.boolean.opBoolean","SPLIT",FACE,{"disambiguationData":[TD([makeQuery(id+"F7.opExtrude","SWEPT_FACE",FACE,{"disambiguationData":[OSD([subQ2])]})])],"derivedFrom":makeQuery(id+"F7.opExtrude","CAP_FACE",FACE,{"disambiguationData":[OSD([sQuery(id+"F6.wireOp",EDGE,"E1.bottom"),subQ2,subQ1,subQ0])],"isStart":false})});}
            var sketch = newSketch(context, id + "F12", { "sketchPlane" : qUnion([Q0])});
            skLineSegment(sketch, "E31.bottom", {"start": v(41.65, 44.68) * mm, "end": v(58.33, 44.68) * mm});
            skLineSegment(sketch, "E31.top", {"start": v(41.65, 28) * mm, "end": v(58.33, 28) * mm});
            skLineSegment(sketch, "E31.left", {"start": v(41.65, 44.68) * mm, "end": v(41.65, 28) * mm});
            skLineSegment(sketch, "E31.right", {"start": v(58.33, 44.68) * mm, "end": v(58.33, 28) * mm});
            skSolve(sketch);
        }
        {
            var Q0;
            Q0=makeQuery(id+"F12.imprint","IMPRINT",FACE,{"disambiguationData":[TD([[makeQuery(id+"F12.imprint","IMPRINT",EDGE,{"derivedFrom":sQuery(id+"F12.wireOp",EDGE,"E31.bottom")}),-1.0]])]});
            extrude(context, id + "F13", {"entities" : qUnion([Q0]), "operationType" : NewBodyOperationType.ADD, "depth" : 0.76 * mm, "offsetDistance" : 25.4 * mm});
        }
        {
            var Q0;
            Q0=makeQuery(id+"F13.opExtrude","CAP_FACE",FACE,{"disambiguationData":[OSD([sQuery(id+"F12.wireOp",EDGE,"E31.bottom"),sQuery(id+"F12.wireOp",EDGE,"E31.top"),sQuery(id+"F12.wireOp",EDGE,"E31.left"),sQuery(id+"F12.wireOp",EDGE,"E31.right")])],"isStart":false});
            var sketch = newSketch(context, id + "F14", { "sketchPlane" : qUnion([Q0])});
            skLineSegment(sketch, "E32.bottom", {"start": v(42.37, 43.96) * mm, "end": v(57.61, 43.96) * mm});
            skLineSegment(sketch, "E32.top", {"start": v(42.37, 29.23) * mm, "end": v(57.61, 29.23) * mm});
            skLineSegment(sketch, "E32.left", {"start": v(42.37, 43.96) * mm, "end": v(42.37, 29.23) * mm});
            skLineSegment(sketch, "E32.right", {"start": v(57.61, 43.96) * mm, "end": v(57.61, 29.23) * mm});
            skPoint(sketch, "E32.middle", {"position": v(50, 36.6) * mm});
            skPoint(sketch, "E32.middle.positionSnap0", {"position": v(50, 44.68) * mm});
            skPoint(sketch, "E32.centerSnap0", {"position": v(50, 44.68) * mm});
            skSolve(sketch);
        }
        {
            var Q0;
            Q0 = qSketchRegion(id + "F14", true);
            extrude(context, id + "F15", {"entities" : qUnion([Q0]), "operationType" : NewBodyOperationType.REMOVE, "oppositeDirection" : true, "depth" : 0.76 * mm, "offsetDistance" : 25.4 * mm});
        }
        {
            var Q0;
            Q0=makeQuery(id+"F15.boolean.opBoolean","COPY",EDGE,{"derivedFrom":makeQuery(id+"F15.opExtrude","SWEPT_EDGE",EDGE,{"disambiguationData":[OSD([sQuery(id+"F14.wireOp",EDGE,"E32.bottom"),sQuery(id+"F14.wireOp",EDGE,"E32.right")])]})});
            var Q1;
            Q1=makeQuery(id+"F15.boolean.opBoolean","COPY",EDGE,{"derivedFrom":makeQuery(id+"F15.opExtrude","SWEPT_EDGE",EDGE,{"disambiguationData":[OSD([sQuery(id+"F14.wireOp",EDGE,"E32.bottom"),sQuery(id+"F14.wireOp",EDGE,"E32.left")])]})});
            var Q2;
            Q2=makeQuery(id+"F15.boolean.opBoolean","COPY",EDGE,{"derivedFrom":makeQuery(id+"F15.opExtrude","SWEPT_EDGE",EDGE,{"disambiguationData":[OSD([sQuery(id+"F14.wireOp",EDGE,"E32.top"),sQuery(id+"F14.wireOp",EDGE,"E32.left")])]})});
            var Q3;
            Q3=makeQuery(id+"F15.boolean.opBoolean","COPY",EDGE,{"derivedFrom":makeQuery(id+"F15.opExtrude","SWEPT_EDGE",EDGE,{"disambiguationData":[OSD([sQuery(id+"F14.wireOp",EDGE,"E32.top"),sQuery(id+"F14.wireOp",EDGE,"E32.right")])]})});
            var Q4;
            Q4=makeQuery(id+"F13.opExtrude","SWEPT_EDGE",EDGE,{"disambiguationData":[OSD([sQuery(id+"F12.wireOp",EDGE,"E31.bottom"),sQuery(id+"F12.wireOp",EDGE,"E31.left")])]});
            var Q5;
            Q5=makeQuery(id+"F13.opExtrude","SWEPT_EDGE",EDGE,{"disambiguationData":[OSD([sQuery(id+"F12.wireOp",EDGE,"E31.bottom"),sQuery(id+"F12.wireOp",EDGE,"E31.right")])]});
            var Q6;
            Q6=makeQuery(id+"F13.opExtrude","SWEPT_EDGE",EDGE,{"disambiguationData":[OSD([sQuery(id+"F12.wireOp",EDGE,"E31.top"),sQuery(id+"F12.wireOp",EDGE,"E31.left")])]});
            var Q7;
            Q7=makeQuery(id+"F13.opExtrude","SWEPT_EDGE",EDGE,{"disambiguationData":[OSD([sQuery(id+"F12.wireOp",EDGE,"E31.top"),sQuery(id+"F12.wireOp",EDGE,"E31.right")])]});
            fillet(context, id + "F16", {"entities" : qUnion([Q0, Q1, Q2, Q3, Q4, Q5, Q6, Q7]), "radius" : 5.08 * mm, "tangentPropagation" : true, "allowEdgeOverflow" : false});
        }
        {
            var Q0;
            Q0=makeQuery(id+"F15.boolean.opBoolean","COPY",FACE,{"derivedFrom":makeQuery(id+"F15.opExtrude","CAP_FACE",FACE,{"disambiguationData":[OSD([sQuery(id+"F14.wireOp",EDGE,"E32.bottom"),sQuery(id+"F14.wireOp",EDGE,"E32.top"),sQuery(id+"F14.wireOp",EDGE,"E32.left"),sQuery(id+"F14.wireOp",EDGE,"E32.right")])],"isStart":false})});
            var sketch = newSketch(context, id + "F17", { "sketchPlane" : qUnion([Q0])});
            skLineSegment(sketch, "E33.bottom", {"start": v(46.13, 39.74) * mm, "end": v(53.86, 39.74) * mm});
            skLineSegment(sketch, "E33.top", {"start": v(46.13, 33.13) * mm, "end": v(53.86, 33.13) * mm});
            skLineSegment(sketch, "E33.left", {"start": v(46.13, 39.74) * mm, "end": v(46.13, 33.13) * mm});
            skLineSegment(sketch, "E33.right", {"start": v(53.86, 39.74) * mm, "end": v(53.86, 33.13) * mm});
            skSolve(sketch);
        }
        {
            var Q0;
            Q0=makeQuery(id+"F17.imprint","IMPRINT",FACE,{"disambiguationData":[TD([[makeQuery(id+"F17.imprint","IMPRINT",EDGE,{"derivedFrom":sQuery(id+"F17.wireOp",EDGE,"E33.bottom")}),-1.0]])]});
            extrude(context, id + "F18", {"entities" : qUnion([Q0]), "operationType" : NewBodyOperationType.REMOVE, "oppositeDirection" : true, "depth" : 0.25 * mm, "offsetDistance" : 25.4 * mm});
        }
        {
            var Q0;
            Q0=makeQuery(id+"F18.boolean.opBoolean","COPY",EDGE,{"derivedFrom":makeQuery(id+"F18.opExtrude","CAP_EDGE",EDGE,{"disambiguationData":[OSD([sQuery(id+"F17.wireOp",EDGE,"E33.right")])],"isStart":false})});
            var Q1;
            Q1=makeQuery(id+"F18.boolean.opBoolean","COPY",EDGE,{"derivedFrom":makeQuery(id+"F18.opExtrude","CAP_EDGE",EDGE,{"disambiguationData":[OSD([sQuery(id+"F17.wireOp",EDGE,"E33.bottom")])],"isStart":false})});
            var Q2;
            Q2=makeQuery(id+"F18.boolean.opBoolean","COPY",EDGE,{"derivedFrom":makeQuery(id+"F18.opExtrude","CAP_EDGE",EDGE,{"disambiguationData":[OSD([sQuery(id+"F17.wireOp",EDGE,"E33.top")])],"isStart":false})});
            var Q3;
            Q3=makeQuery(id+"F18.boolean.opBoolean","COPY",EDGE,{"derivedFrom":makeQuery(id+"F18.opExtrude","CAP_EDGE",EDGE,{"disambiguationData":[OSD([sQuery(id+"F17.wireOp",EDGE,"E33.left")])],"isStart":false})});
            chamfer(context, id + "F19", {"entities" : qUnion([Q0, Q1, Q2, Q3]), "width" : 1.27 * mm, "tangentPropagation" : true});
        }
        {
            var Q0;
            Q0=makeQuery(id+"F19.opChamfer","BLEND_EDGE",EDGE,{"blendedFrom":[makeQuery(id+"F18.boolean.opBoolean","COPY",EDGE,{"derivedFrom":makeQuery(id+"F18.opExtrude","CAP_EDGE",EDGE,{"disambiguationData":[OSD([sQuery(id+"F17.wireOp",EDGE,"E33.bottom")])],"isStart":false})}),makeQuery(id+"F18.boolean.opBoolean","COPY",EDGE,{"derivedFrom":makeQuery(id+"F18.opExtrude","CAP_EDGE",EDGE,{"disambiguationData":[OSD([sQuery(id+"F17.wireOp",EDGE,"E33.left")])],"isStart":false})})],"blendedInto":[]});
            var Q1;
            Q1=makeQuery(id+"F19.opChamfer","BLEND_EDGE",EDGE,{"blendedFrom":[makeQuery(id+"F18.boolean.opBoolean","COPY",EDGE,{"derivedFrom":makeQuery(id+"F18.opExtrude","CAP_EDGE",EDGE,{"disambiguationData":[OSD([sQuery(id+"F17.wireOp",EDGE,"E33.bottom")])],"isStart":false})}),makeQuery(id+"F18.boolean.opBoolean","COPY",EDGE,{"derivedFrom":makeQuery(id+"F18.opExtrude","CAP_EDGE",EDGE,{"disambiguationData":[OSD([sQuery(id+"F17.wireOp",EDGE,"E33.right")])],"isStart":false})})],"blendedInto":[]});
            var Q2;
            Q2=makeQuery(id+"F19.opChamfer","BLEND_EDGE",EDGE,{"blendedFrom":[makeQuery(id+"F18.boolean.opBoolean","COPY",EDGE,{"derivedFrom":makeQuery(id+"F18.opExtrude","CAP_EDGE",EDGE,{"disambiguationData":[OSD([sQuery(id+"F17.wireOp",EDGE,"E33.top")])],"isStart":false})}),makeQuery(id+"F18.boolean.opBoolean","COPY",EDGE,{"derivedFrom":makeQuery(id+"F18.opExtrude","CAP_EDGE",EDGE,{"disambiguationData":[OSD([sQuery(id+"F17.wireOp",EDGE,"E33.right")])],"isStart":false})})],"blendedInto":[]});
            var Q3;
            Q3=makeQuery(id+"F19.opChamfer","BLEND_EDGE",EDGE,{"blendedFrom":[makeQuery(id+"F18.boolean.opBoolean","COPY",EDGE,{"derivedFrom":makeQuery(id+"F18.opExtrude","CAP_EDGE",EDGE,{"disambiguationData":[OSD([sQuery(id+"F17.wireOp",EDGE,"E33.top")])],"isStart":false})}),makeQuery(id+"F18.boolean.opBoolean","COPY",EDGE,{"derivedFrom":makeQuery(id+"F18.opExtrude","CAP_EDGE",EDGE,{"disambiguationData":[OSD([sQuery(id+"F17.wireOp",EDGE,"E33.left")])],"isStart":false})})],"blendedInto":[]});
            fillet(context, id + "F20", {"entities" : qUnion([Q0, Q1, Q2, Q3]), "radius" : 0.76 * mm, "tangentPropagation" : true, "allowEdgeOverflow" : false});
        }
        {
            var Q0;
            {var subQ0=sQuery(id+"F6.wireOp",EDGE,"E1.right");var subQ1=sQuery(id+"F6.wireOp",EDGE,"E1.left");var subQ2=sQuery(id+"F6.wireOp",EDGE,"E1.top");Q0=makeQuery(id+"F10.boolean.opBoolean","SPLIT",FACE,{"disambiguationData":[TD([makeQuery(id+"F7.opExtrude","SWEPT_FACE",FACE,{"disambiguationData":[OSD([subQ2])]})])],"derivedFrom":makeQuery(id+"F7.opExtrude","CAP_FACE",FACE,{"disambiguationData":[OSD([sQuery(id+"F6.wireOp",EDGE,"E1.bottom"),subQ2,subQ1,subQ0])],"isStart":false})});}
            var sketch = newSketch(context, id + "F21", { "sketchPlane" : qUnion([Q0])});
            skLineSegment(sketch, "E34", {"start": v(41.65, 36.34) * mm, "end": v(58.33, 36.34) * mm});
            skLineSegment(sketch, "E35", {"start": v(29.48, 36.34) * mm, "end": v(70.12, 36.34) * mm});
            skLineSegment(sketch, "E36", {"start": v(29.48, 38.36) * mm, "end": v(70.12, 38.36) * mm});
            skLineSegment(sketch, "E37", {"start": v(41.65, 39.6) * mm, "end": v(41.65, 36.34) * mm});
            skLineSegment(sketch, "E38", {"start": v(58.33, 36.34) * mm, "end": v(58.33, 39.6) * mm});
            skSolve(sketch);
        }
        {
            var Q0;
            {var subQ0=sQuery(id+"F21.wireOp",EDGE,"E37");var subQ7=sQuery(id+"F21.wireOp",EDGE,"E36");var subQ8=makeQuery(id+"F21.imprint","INTERSECT",VERTEX,{"derivedFrom":[subQ7,subQ0]});Q0=makeQuery(id+"F21.imprint","IMPRINT",FACE,{"disambiguationData":[TD([[makeQuery(id+"F21.imprint","IMPRINT",EDGE,{"disambiguationData":[TD([[subQ8,-1.0]])],"derivedFrom":subQ0}),-1.0]])]});}
            var Q1;
            {var subQ0=sQuery(id+"F21.wireOp",EDGE,"E38");var subQ7=sQuery(id+"F21.wireOp",EDGE,"E36");var subQ9=makeQuery(id+"F21.imprint","INTERSECT",VERTEX,{"derivedFrom":[subQ7,subQ0]});Q1=makeQuery(id+"F21.imprint","IMPRINT",FACE,{"disambiguationData":[TD([[makeQuery(id+"F21.imprint","IMPRINT",EDGE,{"disambiguationData":[TD([[subQ9,-1.0]])],"derivedFrom":subQ0}),1.0]])]});}
            extrude(context, id + "F22", {"entities" : qUnion([Q0, Q1]), "operationType" : NewBodyOperationType.REMOVE, "oppositeDirection" : true, "depth" : 0.5 * mm, "offsetDistance" : 25.4 * mm});
        }
        {
            var Q0;
            {var subQ4=sQuery(id+"F6.wireOp",EDGE,"E1.right");var subQ5=sQuery(id+"F6.wireOp",EDGE,"E1.left");var subQ6=sQuery(id+"F6.wireOp",EDGE,"E1.top");var subQ7=makeQuery(id+"F7.opExtrude","CAP_FACE",FACE,{"disambiguationData":[OSD([sQuery(id+"F6.wireOp",EDGE,"E1.bottom"),subQ6,subQ5,subQ4])],"isStart":false});var subQ13=makeQuery(id+"F7.opExtrude","SWEPT_FACE",FACE,{"disambiguationData":[OSD([subQ6])]});Q0=makeQuery(id+"F22.boolean.opBoolean","SPLIT",FACE,{"disambiguationData":[TD([subQ13])],"derivedFrom":makeQuery(id+"F10.boolean.opBoolean","SPLIT",FACE,{"disambiguationData":[TD([subQ13])],"derivedFrom":subQ7})});}
            var sketch = newSketch(context, id + "F23", { "sketchPlane" : qUnion([Q0])});
            skLineSegment(sketch, "E39", {"start": v(48.9, 54.88) * mm, "end": v(48.9, 16.3) * mm});
            skLineSegment(sketch, "E40", {"start": v(50.8, 54.88) * mm, "end": v(50.8, 16.3) * mm});
            skLineSegment(sketch, "E41", {"start": v(48.9, 54.88) * mm, "end": v(50.8, 54.88) * mm});
            skLineSegment(sketch, "E42", {"start": v(48.9, 44.68) * mm, "end": v(50.8, 44.68) * mm});
            skPoint(sketch, "E42.endSnap0", {"position": v(50, 44.68) * mm});
            skLineSegment(sketch, "E43", {"start": v(48.9, 16.3) * mm, "end": v(50.8, 16.3) * mm});
            skLineSegment(sketch, "E44", {"start": v(48.9, 28.05) * mm, "end": v(50.8, 28.05) * mm});
            skSolve(sketch);
        }
        {
            var Q0;
            {var subQ0=sQuery(id+"F23.wireOp",EDGE,"E41");Q0=makeQuery(id+"F23.imprint","IMPRINT",FACE,{"disambiguationData":[TD([[makeQuery(id+"F23.imprint","IMPRINT",EDGE,{"derivedFrom":subQ0}),-1.0]])]});}
            var Q1;
            {var subQ0=sQuery(id+"F23.wireOp",EDGE,"E43");Q1=makeQuery(id+"F23.imprint","IMPRINT",FACE,{"disambiguationData":[TD([[makeQuery(id+"F23.imprint","IMPRINT",EDGE,{"derivedFrom":subQ0}),1.0]])]});}
            extrude(context, id + "F24", {"entities" : qUnion([Q0, Q1]), "operationType" : NewBodyOperationType.REMOVE, "oppositeDirection" : true, "depth" : 0.5 * mm, "offsetDistance" : 25.4 * mm});
        }
        {
            var Q0;
            Q0=makeQuery(id+"F1.opExtrude","CAP_FACE",FACE,{"disambiguationData":[OSD([sQuery(id+"F0.wireOp",EDGE,"E0.bottom"),sQuery(id+"F0.wireOp",EDGE,"E0.top"),sQuery(id+"F0.wireOp",EDGE,"E0.left"),sQuery(id+"F0.wireOp",EDGE,"E0.right")])],"isStart":true});
            var sketch = newSketch(context, id + "F25", { "sketchPlane" : qUnion([Q0])});
            skLineSegment(sketch, "E45.bottom", {"start": v(-29.35, -53.85) * mm, "end": v(2.86, -53.85) * mm});
            skLineSegment(sketch, "E45.top", {"start": v(-29.35, -48) * mm, "end": v(2.86, -48) * mm});
            skLineSegment(sketch, "E45.left", {"start": v(-29.35, -53.85) * mm, "end": v(-29.35, -48) * mm});
            skLineSegment(sketch, "E45.right", {"start": v(2.86, -53.85) * mm, "end": v(2.86, -48) * mm});
            skSolve(sketch);
        }
        {
            var Q0;
            {var subQ0=sQuery(id+"F25.wireOp",EDGE,"E45.top");Q0=makeQuery(id+"F25.imprint","IMPRINT",FACE,{"disambiguationData":[TD([[makeQuery(id+"F25.imprint","IMPRINT",EDGE,{"derivedFrom":subQ0}),-1.0]])]});}
            var Q1;
            {var subQ0=sQuery(id+"F25.wireOp",EDGE,"E45.bottom");Q1=makeQuery(id+"F25.imprint","IMPRINT",FACE,{"disambiguationData":[TD([[makeQuery(id+"F25.imprint","IMPRINT",EDGE,{"derivedFrom":subQ0}),1.0]])]});}
            extrude(context, id + "F26", {"entities" : qUnion([Q0, Q1]), "operationType" : NewBodyOperationType.REMOVE, "oppositeDirection" : true, "depth" : 25.4 * mm, "offsetDistance" : 25.4 * mm});
        }
    });
